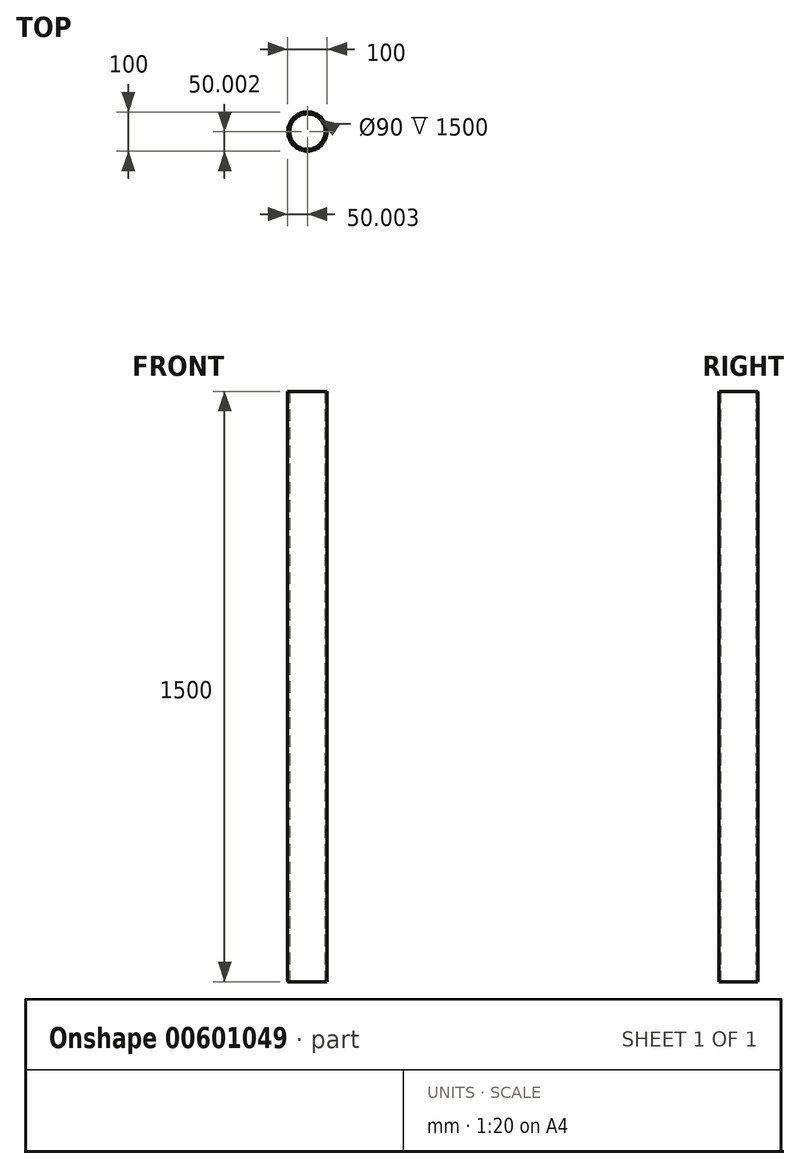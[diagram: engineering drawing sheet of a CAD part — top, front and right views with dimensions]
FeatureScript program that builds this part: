
annotation { "Feature Type Name" : "Feature", "Feature Type Description" : "" }
export const myFeature = defineFeature(function(context is Context, id is Id, definition is map)
    precondition{}
    {
        {
            var Q0;
            Q0=qCreatedBy(makeId("Top.planeOp"),FACE);
            var sketch = newSketch(context, id + "F0", { "sketchPlane" : qUnion([Q0])});
            skCircle(sketch, "E0", {"center": v(-131.27, -49.5) * mm, "radius": 50 * mm});
            skCircle(sketch, "E1", {"center": v(-131.27, -49.5) * mm, "radius": 45 * mm});
            skSolve(sketch);
        }
        {
            var Q0;
            Q0 = qSketchRegion(id + "F0", true);
            extrude(context, id + "F1", {"entities" : qUnion([Q0]), "depth" : 1500 * mm, "offsetDistance" : 25 * mm});
        }
    });
